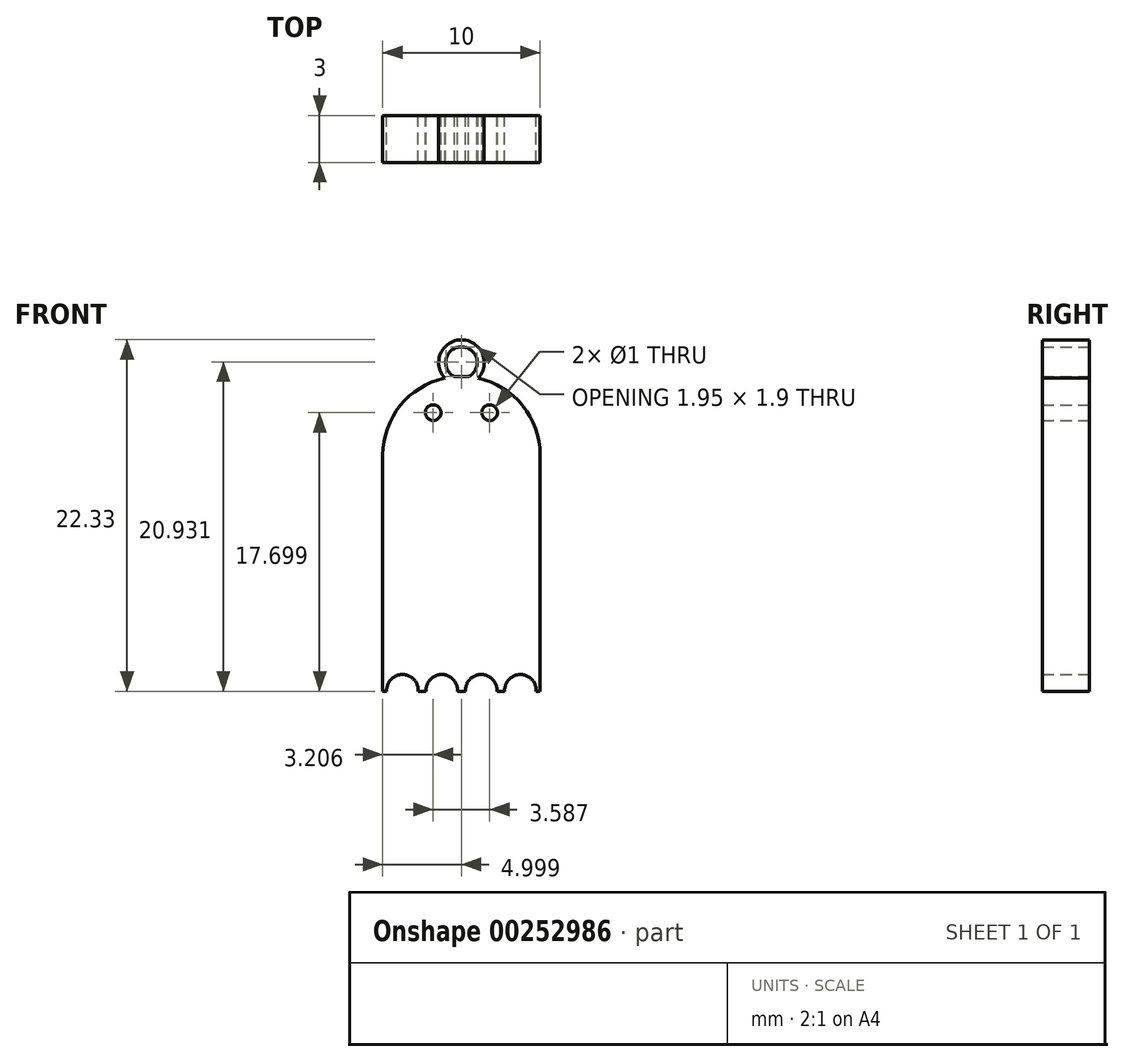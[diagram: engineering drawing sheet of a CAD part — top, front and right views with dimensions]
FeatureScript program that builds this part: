
annotation { "Feature Type Name" : "Feature", "Feature Type Description" : "" }
export const myFeature = defineFeature(function(context is Context, id is Id, definition is map)
    precondition{}
    {
        {
            var Q0;
            Q0=qCreatedBy(makeId("Front.planeOp"),FACE);
            var sketch = newSketch(context, id + "F0", { "sketchPlane" : qUnion([Q0])});
            skArc(sketch, "E0", {"start": v(-8.6, 40.3) * mm, "mid": v(-9.7, 43.43) * mm, "end": v(-12.53, 45.18) * mm});
            skLineSegment(sketch, "E1", {"start": v(-18.6, 40.3) * mm, "end": v(-18.6, 25.3) * mm});
            skLineSegment(sketch, "E2", {"start": v(-8.6, 40.3) * mm, "end": v(-8.6, 25.3) * mm});
            skLineSegment(sketch, "E3", {"start": v(-8.6, 25.3) * mm, "end": v(-8.85, 25.3) * mm});
            skArc(sketch, "E4", {"start": v(-12.53, 45.18) * mm, "mid": v(-13.6, 47.62) * mm, "end": v(-14.65, 45.18) * mm});
            skLineSegment(sketch, "E5", {"start": v(-18.6, 25.3) * mm, "end": v(-18.34, 25.3) * mm});
            skLineSegment(sketch, "E6", {"start": v(-16.34, 25.3) * mm, "end": v(-15.84, 25.3) * mm});
            skArc(sketch, "E7", {"start": v(-13.85, 25.3) * mm, "mid": v(-14.84, 26.35) * mm, "end": v(-15.84, 25.3) * mm});
            skArc(sketch, "E8.MirrorCS", {"start": v(-13.33, 25.3) * mm, "mid": v(-12.34, 26.35) * mm, "end": v(-11.34, 25.3) * mm});
            skArc(sketch, "E9.MirrorCS", {"start": v(-18.33, 25.3) * mm, "mid": v(-17.34, 26.35) * mm, "end": v(-16.34, 25.3) * mm});
            skArc(sketch, "E10.MirrorCS", {"start": v(-8.85, 25.3) * mm, "mid": v(-9.84, 26.35) * mm, "end": v(-10.84, 25.3) * mm});
            skArc(sketch, "E11", {"start": v(-13.15, 45.27) * mm, "mid": v(-13.6, 47.17) * mm, "end": v(-14.03, 45.27) * mm});
            skLineSegment(sketch, "E12.trimOffspring", {"start": v(-10.84, 25.3) * mm, "end": v(-11.34, 25.3) * mm});
            skLineSegment(sketch, "E13.trimOffspring", {"start": v(-13.33, 25.3) * mm, "end": v(-13.85, 25.3) * mm});
            skLineSegment(sketch, "E14.trimOffspring", {"start": v(-15.84, 25.3) * mm, "end": v(-16.34, 25.3) * mm});
            skLineSegment(sketch, "E15.trimOffspring", {"start": v(-18.33, 25.3) * mm, "end": v(-18.6, 25.3) * mm});
            skArc(sketch, "E16.trimOffspring", {"start": v(-14.65, 45.18) * mm, "mid": v(-17.48, 43.43) * mm, "end": v(-18.6, 40.3) * mm});
            skArc(sketch, "E17.trimOffspring", {"start": v(-13.15, 45.27) * mm, "mid": v(-13.6, 45.3) * mm, "end": v(-14.03, 45.27) * mm});
            skCircle(sketch, "E18", {"center": v(-15.38, 42.99) * mm, "radius": 0.5 * mm});
            skCircle(sketch, "E19.MirrorC", {"center": v(-11.8, 42.99) * mm, "radius": 0.5 * mm});
            skSolve(sketch);
        }
        {
            var Q0;
            Q0=makeQuery(id+"F0.imprint","IMPRINT",FACE,{"disambiguationData":[TD([[makeQuery(id+"F0.imprint","IMPRINT",EDGE,{"derivedFrom":sQuery(id+"F0.wireOp",EDGE,"E0")}),1.0]])]});
            extrude(context, id + "F1", {"entities" : qUnion([Q0]), "depth" : 3 * mm});
        }
    });
